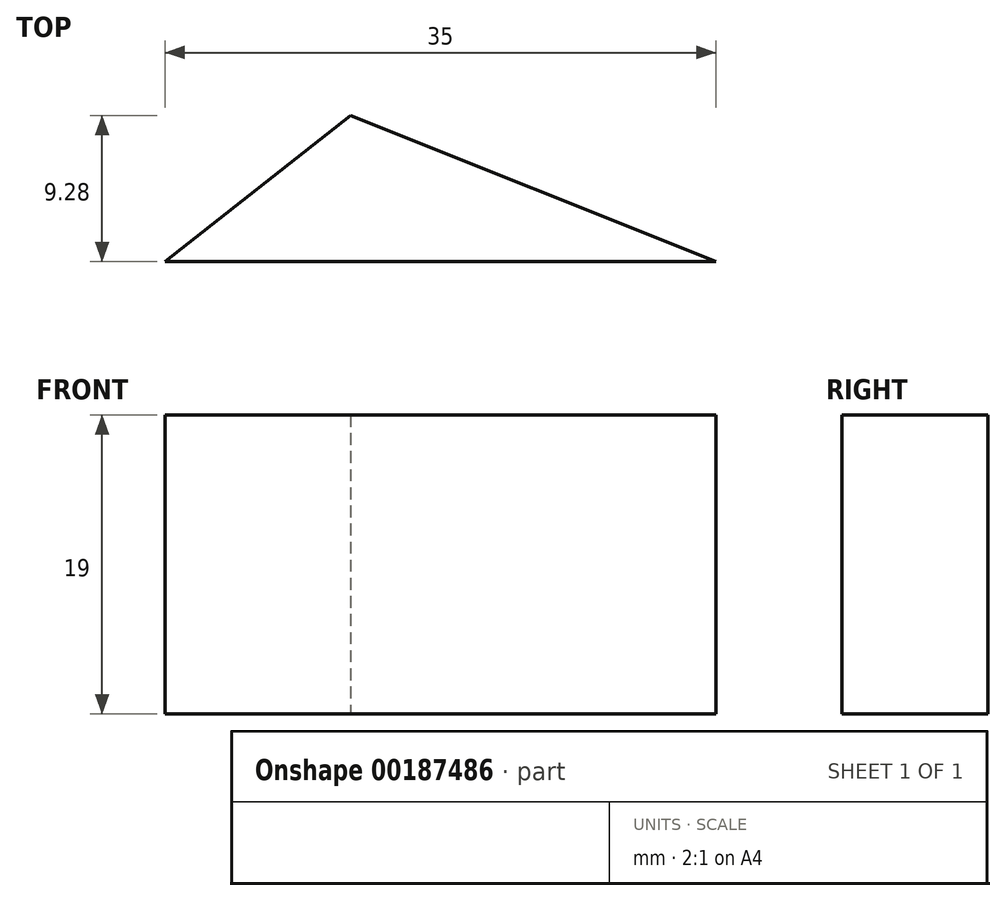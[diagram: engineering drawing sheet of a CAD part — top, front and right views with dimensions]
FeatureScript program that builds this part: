
annotation { "Feature Type Name" : "Feature", "Feature Type Description" : "" }
export const myFeature = defineFeature(function(context is Context, id is Id, definition is map)
    precondition{}
    {
        {
            var Q0;
            Q0=qCreatedBy(makeId("Top.planeOp"),FACE);
            var sketch = newSketch(context, id + "F0", { "sketchPlane" : qUnion([Q0])});
            skLineSegment(sketch, "E0", {"start": v(0, 0) * mm, "end": v(35, 0) * mm});
            skLineSegment(sketch, "E1", {"start": v(0, 0) * mm, "end": v(11.79, 9.28) * mm});
            skLineSegment(sketch, "E2", {"start": v(11.79, 9.28) * mm, "end": v(35, 0) * mm});
            skSolve(sketch);
        }
        {
            var Q0;
            Q0=makeQuery(id+"F0.imprint","IMPRINT",FACE,{"disambiguationData":[TD([[makeQuery(id+"F0.imprint","IMPRINT",EDGE,{"derivedFrom":sQuery(id+"F0.wireOp",EDGE,"E0")}),1.0]])]});
            extrude(context, id + "F1", {"entities" : qUnion([Q0]), "depth" : 19 * mm});
        }
    });
